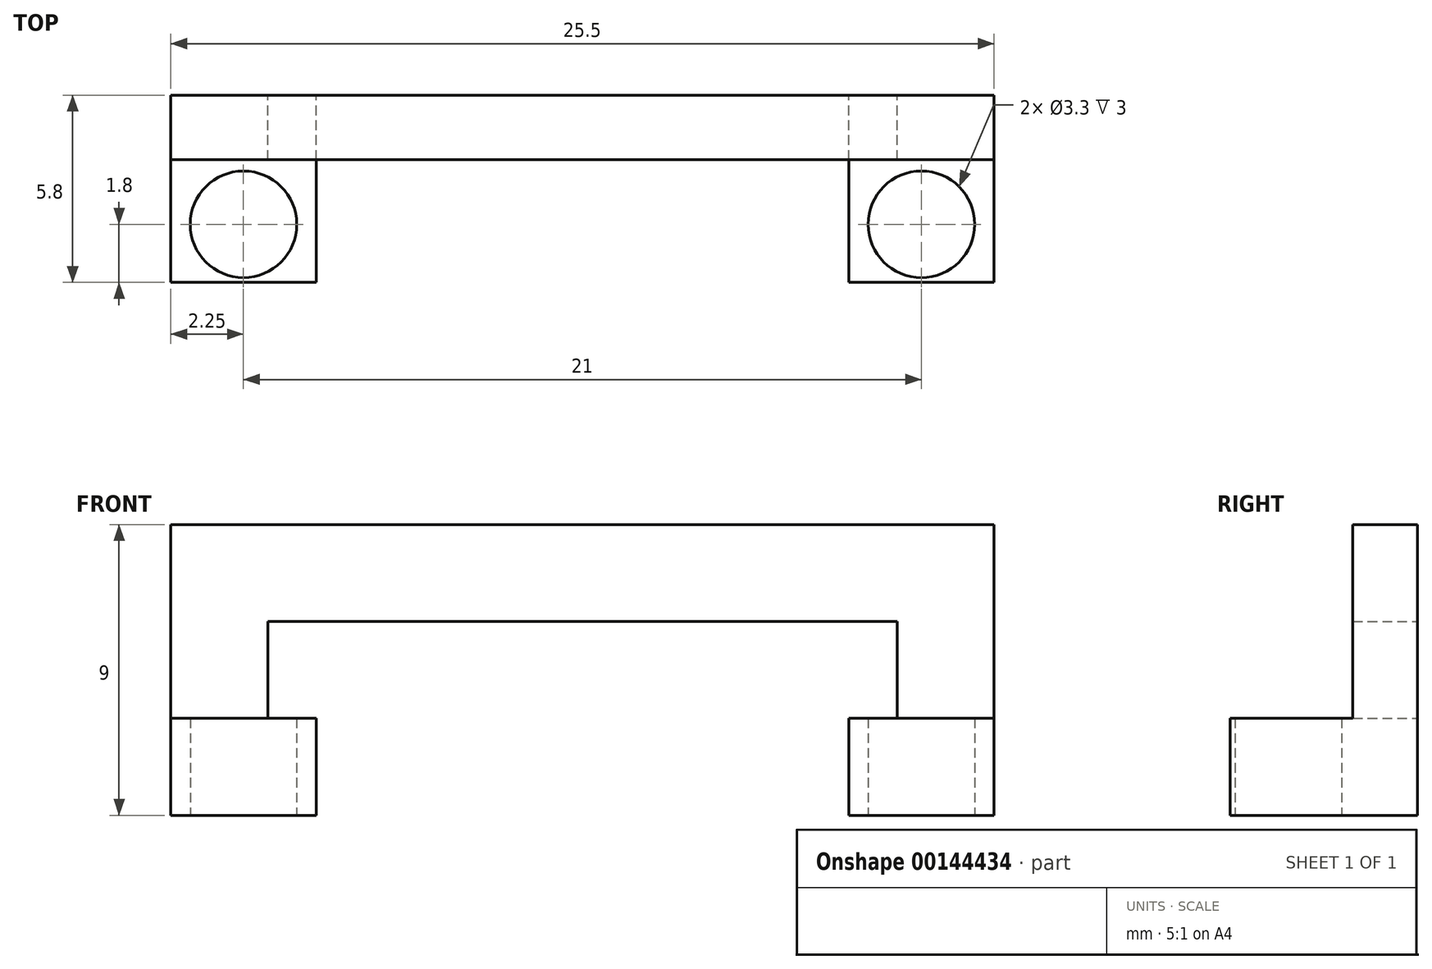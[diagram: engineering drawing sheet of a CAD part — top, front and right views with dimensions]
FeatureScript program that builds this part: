
annotation { "Feature Type Name" : "Feature", "Feature Type Description" : "" }
export const myFeature = defineFeature(function(context is Context, id is Id, definition is map)
    precondition{}
    {
        {
            var Q0;
            Q0=qCreatedBy(makeId("Front.planeOp"),FACE);
            var sketch = newSketch(context, id + "F0", { "sketchPlane" : qUnion([Q0])});
            skLineSegment(sketch, "E0.bottom", {"start": v(0, 0) * mm, "end": v(-9.75, 0) * mm});
            skLineSegment(sketch, "E0.top", {"start": v(0, 3) * mm, "end": v(-9.75, 3) * mm});
            skLineSegment(sketch, "E0.left", {"start": v(0, 0) * mm, "end": v(0, 3) * mm});
            skLineSegment(sketch, "E0.right", {"start": v(-9.75, 0) * mm, "end": v(-9.75, 3) * mm});
            skLineSegment(sketch, "E1.bottom", {"start": v(-9.75, 3) * mm, "end": v(-12.75, 3) * mm});
            skLineSegment(sketch, "E1.top", {"start": v(-9.75, -3) * mm, "end": v(-12.75, -3) * mm});
            skLineSegment(sketch, "E1.left", {"start": v(-9.75, 3) * mm, "end": v(-9.75, -3) * mm});
            skLineSegment(sketch, "E1.right", {"start": v(-12.75, 3) * mm, "end": v(-12.75, -3) * mm});
            skLineSegment(sketch, "E2.bottom", {"start": v(-12.75, -3) * mm, "end": v(-8.25, -3) * mm});
            skLineSegment(sketch, "E2.top", {"start": v(-12.75, -6) * mm, "end": v(-8.25, -6) * mm});
            skLineSegment(sketch, "E2.left", {"start": v(-12.75, -3) * mm, "end": v(-12.75, -6) * mm});
            skLineSegment(sketch, "E2.right", {"start": v(-8.25, -3) * mm, "end": v(-8.25, -6) * mm});
            skLineSegment(sketch, "E3.MirrorCS", {"start": v(-12.75, -3) * mm, "end": v(-12.75, 0) * mm});
            skLineSegment(sketch, "E4.MirrorCS", {"start": v(-12.75, 0) * mm, "end": v(-8.25, 0) * mm});
            skLineSegment(sketch, "E5.MirrorCS", {"start": v(-12.75, -9) * mm, "end": v(-12.75, -3) * mm});
            skLineSegment(sketch, "E6.MirrorCS", {"start": v(-9.75, -9) * mm, "end": v(-9.75, -3) * mm});
            skLineSegment(sketch, "E7.MirrorCS", {"start": v(0, 0) * mm, "end": v(9.75, 0) * mm});
            skLineSegment(sketch, "E8.MirrorCS", {"start": v(0, 3) * mm, "end": v(9.75, 3) * mm});
            skLineSegment(sketch, "E9.MirrorCS", {"start": v(9.75, 3) * mm, "end": v(9.75, -3) * mm});
            skLineSegment(sketch, "E10.MirrorCS", {"start": v(9.75, 3) * mm, "end": v(12.75, 3) * mm});
            skLineSegment(sketch, "E11.MirrorCS", {"start": v(12.75, 3) * mm, "end": v(12.75, -3) * mm});
            skLineSegment(sketch, "E12.MirrorCS", {"start": v(12.75, -3) * mm, "end": v(12.75, -6) * mm});
            skLineSegment(sketch, "E13.MirrorCS", {"start": v(12.75, -6) * mm, "end": v(8.25, -6) * mm});
            skLineSegment(sketch, "E14.MirrorCS", {"start": v(8.25, -3) * mm, "end": v(8.25, -6) * mm});
            skLineSegment(sketch, "E15.MirrorCS", {"start": v(12.75, -3) * mm, "end": v(8.25, -3) * mm});
            skPoint(sketch, "E16.MirrorCS.end.orphan", {"position": v(-8.25, 0) * mm});
            skPoint(sketch, "E16.MirrorCS.start.orphan", {"position": v(-8.25, -3) * mm});
            skSolve(sketch);
        }
        {
            var Q0;
            Q0 = qSketchRegion(id + "F0", true);
            extrude(context, id + "F1", {"entities" : qUnion([Q0]), "depth" : 2 * mm});
        }
        {
            var Q0;
            Q0=makeQuery(id+"F1.opExtrude","CAP_FACE",FACE,{"disambiguationData":[OSD([sQuery(id+"F0.wireOp",EDGE,"E0.bottom"),sQuery(id+"F0.wireOp",EDGE,"E0.top"),sQuery(id+"F0.wireOp",EDGE,"E1.bottom"),sQuery(id+"F0.wireOp",EDGE,"E1.right"),sQuery(id+"F0.wireOp",EDGE,"E3.MirrorCS"),sQuery(id+"F0.wireOp",EDGE,"E16.MirrorCS"),sQuery(id+"F0.wireOp",EDGE,"E5.MirrorCS"),sQuery(id+"F0.wireOp",EDGE,"E2.top"),sQuery(id+"F0.wireOp",EDGE,"E6.MirrorCS"),sQuery(id+"F0.wireOp",EDGE,"E7.MirrorCS"),sQuery(id+"F0.wireOp",EDGE,"E8.MirrorCS"),sQuery(id+"F0.wireOp",EDGE,"E9.MirrorCS"),sQuery(id+"F0.wireOp",EDGE,"E10.MirrorCS"),sQuery(id+"F0.wireOp",EDGE,"E11.MirrorCS"),sQuery(id+"F0.wireOp",EDGE,"E12.MirrorCS"),sQuery(id+"F0.wireOp",EDGE,"E13.MirrorCS"),sQuery(id+"F0.wireOp",EDGE,"E14.MirrorCS")])],"isStart":false});
            var sketch = newSketch(context, id + "F2", { "sketchPlane" : qUnion([Q0])});
            skLineSegment(sketch, "E17.bottom", {"start": v(-8.25, -6) * mm, "end": v(-12.75, -6) * mm});
            skLineSegment(sketch, "E17.top", {"start": v(-8.25, -3) * mm, "end": v(-12.75, -3) * mm});
            skLineSegment(sketch, "E17.left", {"start": v(-8.25, -6) * mm, "end": v(-8.25, -3) * mm});
            skLineSegment(sketch, "E17.right", {"start": v(-12.75, -6) * mm, "end": v(-12.75, -3) * mm});
            skLineSegment(sketch, "E18.MirrorCS", {"start": v(12.75, -6) * mm, "end": v(12.75, -3) * mm});
            skLineSegment(sketch, "E19.MirrorCS", {"start": v(8.25, -3) * mm, "end": v(12.75, -3) * mm});
            skLineSegment(sketch, "E20.MirrorCS", {"start": v(8.25, -6) * mm, "end": v(8.25, -3) * mm});
            skLineSegment(sketch, "E21.MirrorCS", {"start": v(8.25, -6) * mm, "end": v(12.75, -6) * mm});
            skSolve(sketch);
        }
        {
            var Q0;
            Q0 = qSketchRegion(id + "F2", true);
            extrude(context, id + "F3", {"entities" : qUnion([Q0]), "operationType" : NewBodyOperationType.ADD, "depth" : 3.8 * mm});
        }
        {
            var Q0;
            Q0=makeQuery(id+"F3.boolean.opBoolean","MERGE",FACE,{"derivedFrom":[makeQuery(id+"F1.opExtrude","SWEPT_FACE",FACE,{"disambiguationData":[OSD([sQuery(id+"F0.wireOp",EDGE,"E2.top")])]}),makeQuery(id+"F3.opExtrude","SWEPT_FACE",FACE,{"disambiguationData":[OSD([sQuery(id+"F2.wireOp",EDGE,"E17.bottom")])]})]});
            var sketch = newSketch(context, id + "F4", { "sketchPlane" : qUnion([Q0])});
            skCircle(sketch, "E22", {"center": v(-10.5, 4) * mm, "radius": 1.65 * mm});
            skPoint(sketch, "E22.centerSnap0", {"position": v(-10.5, 5.8) * mm});
            skCircle(sketch, "E23.MirrorC", {"center": v(10.5, 4) * mm, "radius": 1.65 * mm});
            skSolve(sketch);
        }
        {
            var Q0;
            Q0 = qSketchRegion(id + "F4", true);
            extrude(context, id + "F5", {"entities" : qUnion([Q0]), "operationType" : NewBodyOperationType.REMOVE, "endBound" : BoundingType.THROUGH_ALL, "oppositeDirection" : true, "depth" : 25.4 * mm});
        }
    });
